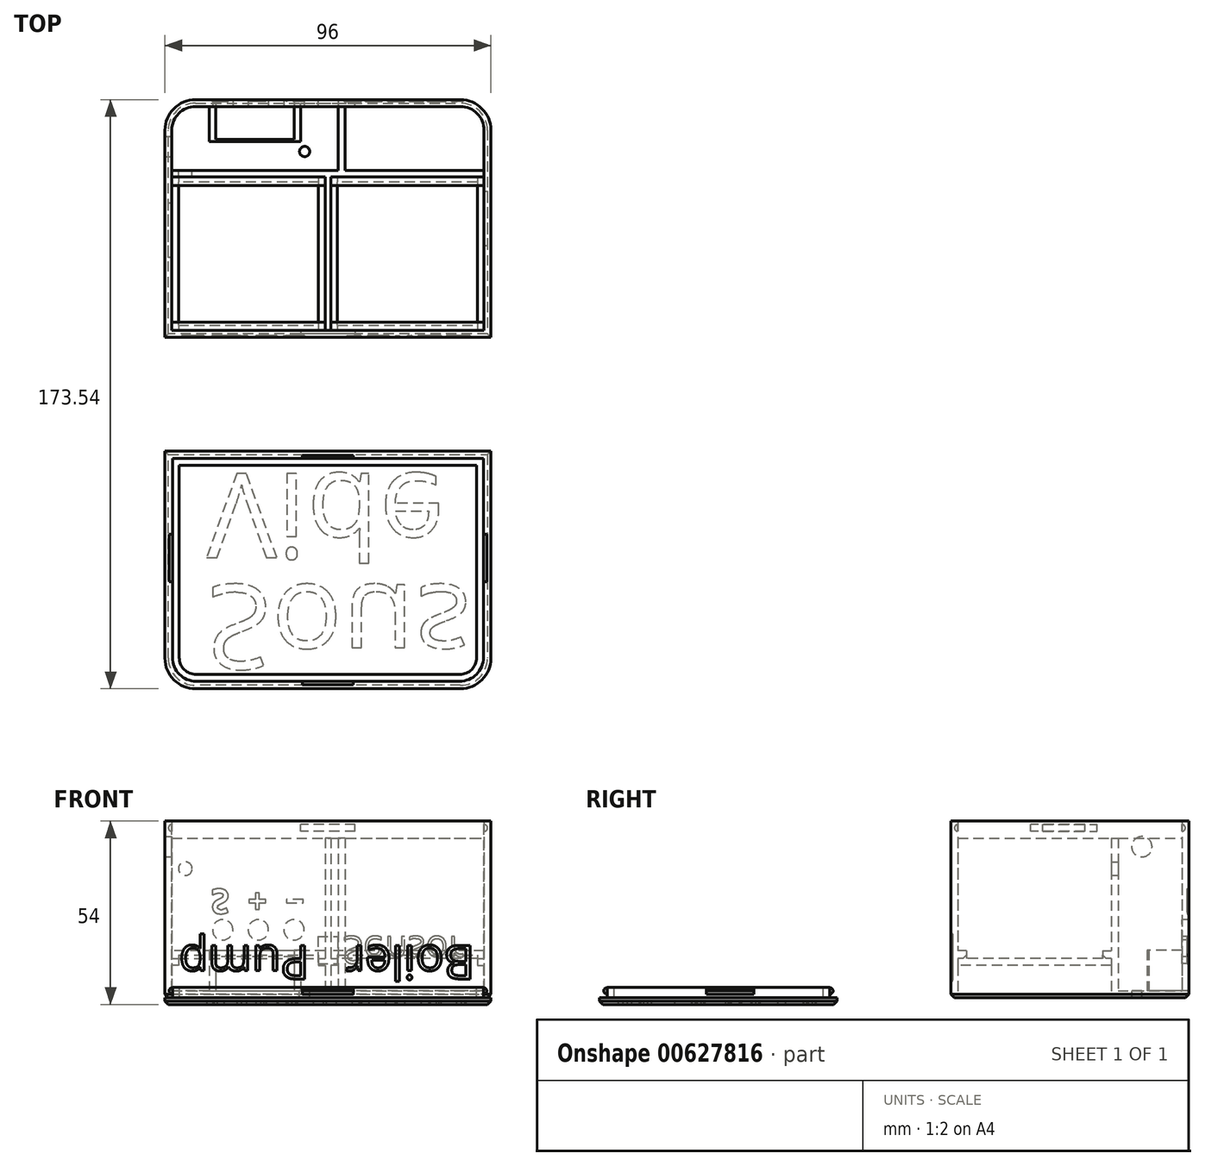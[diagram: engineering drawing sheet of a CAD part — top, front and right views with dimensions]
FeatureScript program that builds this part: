
annotation { "Feature Type Name" : "Feature", "Feature Type Description" : "" }
export const myFeature = defineFeature(function(context is Context, id is Id, definition is map)
    precondition{}
    {
        {
            var Q0;
            Q0=qCreatedBy(makeId("Top.planeOp"),FACE);
            var sketch = newSketch(context, id + "F0", { "sketchPlane" : qUnion([Q0])});
            skLineSegment(sketch, "E0.bottom", {"start": v(48, -35) * mm, "end": v(-48, -35) * mm});
            skLineSegment(sketch, "E0.top", {"start": v(48, 35) * mm, "end": v(-48, 35) * mm});
            skLineSegment(sketch, "E0.left", {"start": v(48, -35) * mm, "end": v(48, 35) * mm});
            skLineSegment(sketch, "E0.right", {"start": v(-48, -35) * mm, "end": v(-48, 35) * mm});
            skPoint(sketch, "E0.middle", {"position": v(0, 0) * mm});
            skLineSegment(sketch, "E1.bottom", {"start": v(48, -138.54) * mm, "end": v(-48, -138.54) * mm});
            skLineSegment(sketch, "E1.top", {"start": v(48, -68.54) * mm, "end": v(-48, -68.54) * mm});
            skLineSegment(sketch, "E1.left", {"start": v(48, -138.54) * mm, "end": v(48, -68.54) * mm});
            skLineSegment(sketch, "E1.right", {"start": v(-48, -138.54) * mm, "end": v(-48, -68.54) * mm});
            skPoint(sketch, "E1.middle", {"position": v(0, -103.54) * mm});
            skPoint(sketch, "E1.middle.positionSnap0", {"position": v(0, -35) * mm});
            skPoint(sketch, "E1.centerSnap0", {"position": v(0, -35) * mm});
            skLineSegment(sketch, "E2.bottom", {"start": v(45.8, -136.34) * mm, "end": v(-45.8, -136.34) * mm});
            skLineSegment(sketch, "E2.top", {"start": v(45.8, -70.74) * mm, "end": v(-45.8, -70.74) * mm});
            skLineSegment(sketch, "E2.left", {"start": v(45.8, -136.34) * mm, "end": v(45.8, -70.74) * mm});
            skLineSegment(sketch, "E2.right", {"start": v(-45.8, -136.34) * mm, "end": v(-45.8, -70.74) * mm});
            skSolve(sketch);
        }
        {
            var Q0;
            Q0=makeQuery(id+"F0.imprint","IMPRINT",FACE,{"disambiguationData":[TD([[makeQuery(id+"F0.imprint","IMPRINT",EDGE,{"derivedFrom":sQuery(id+"F0.wireOp",EDGE,"E0.bottom")}),-1.0]])]});
            extrude(context, id + "F1", {"entities" : qUnion([Q0]), "depth" : 52 * mm, "offsetDistance" : 25 * mm});
        }
        {
            var Q0;
            Q0=makeQuery(id+"F0.imprint","IMPRINT",FACE,{"disambiguationData":[TD([[makeQuery(id+"F0.imprint","IMPRINT",EDGE,{"derivedFrom":sQuery(id+"F0.wireOp",EDGE,"E1.bottom")}),-1.0]])]});
            var Q1;
            Q1=makeQuery(id+"F0.imprint","IMPRINT",FACE,{"disambiguationData":[TD([[makeQuery(id+"F0.imprint","IMPRINT",EDGE,{"derivedFrom":sQuery(id+"F0.wireOp",EDGE,"E2.bottom")}),-1.0]])]});
            extrude(context, id + "F2", {"entities" : qUnion([Q0, Q1]), "oppositeDirection" : true, "depth" : 2 * mm, "offsetDistance" : 25 * mm});
        }
        {
            var Q0;
            Q0=makeQuery(id+"F1.opExtrude","SWEPT_EDGE",EDGE,{"disambiguationData":[OSD([sQuery(id+"F0.wireOp",EDGE,"E0.top"),sQuery(id+"F0.wireOp",EDGE,"E0.right")])]});
            var Q1;
            Q1=makeQuery(id+"F1.opExtrude","SWEPT_EDGE",EDGE,{"disambiguationData":[OSD([sQuery(id+"F0.wireOp",EDGE,"E0.top"),sQuery(id+"F0.wireOp",EDGE,"E0.left")])]});
            var Q2;
            Q2=makeQuery(id+"F2.opExtrude","SWEPT_EDGE",EDGE,{"disambiguationData":[OSD([sQuery(id+"F0.wireOp",EDGE,"E1.bottom"),sQuery(id+"F0.wireOp",EDGE,"E1.right")])]});
            var Q3;
            Q3=makeQuery(id+"F2.opExtrude","SWEPT_EDGE",EDGE,{"disambiguationData":[OSD([sQuery(id+"F0.wireOp",EDGE,"E1.bottom"),sQuery(id+"F0.wireOp",EDGE,"E1.left")])]});
            fillet(context, id + "F3", {"entities" : qUnion([Q0, Q1, Q2, Q3]), "radius" : 9 * mm, "tangentPropagation" : true, "allowEdgeOverflow" : false});
        }
        {
            var Q0;
            Q0=makeQuery(id+"F1.opExtrude","CAP_FACE",FACE,{"disambiguationData":[OSD([sQuery(id+"F0.wireOp",EDGE,"E0.bottom"),sQuery(id+"F0.wireOp",EDGE,"E0.top"),sQuery(id+"F0.wireOp",EDGE,"E0.left"),sQuery(id+"F0.wireOp",EDGE,"E0.right")])],"isStart":false});
            shell(context, id + "F4", {"entities" : qUnion([Q0]), "thickness" : 2 * mm});
        }
        {
            var Q0;
            Q0=makeQuery(id+"F4.opShell","OFFSET_FACE",FACE,{"disambiguationData":[OSD([sQuery(id+"F0.wireOp",EDGE,"E0.bottom"),sQuery(id+"F0.wireOp",EDGE,"E0.top"),sQuery(id+"F0.wireOp",EDGE,"E0.left"),sQuery(id+"F0.wireOp",EDGE,"E0.right")])]});
            var sketch = newSketch(context, id + "F5", { "sketchPlane" : qUnion([Q0])});
            skLineSegment(sketch, "E3", {"start": v(-46, 12.2) * mm, "end": v(46, 12.2) * mm});
            skLineSegment(sketch, "E4", {"start": v(-46, 14.2) * mm, "end": v(46, 14.2) * mm});
            skLineSegment(sketch, "E5", {"start": v(3, 14.2) * mm, "end": v(3, 33) * mm});
            skLineSegment(sketch, "E6", {"start": v(5, 14.2) * mm, "end": v(5, 33) * mm});
            skLineSegment(sketch, "E7.bottom", {"start": v(-0.8, -33) * mm, "end": v(0.8, -33) * mm});
            skLineSegment(sketch, "E7.top", {"start": v(-0.8, 12.2) * mm, "end": v(0.8, 12.2) * mm});
            skLineSegment(sketch, "E7.left", {"start": v(-0.8, -33) * mm, "end": v(-0.8, 12.2) * mm});
            skLineSegment(sketch, "E7.right", {"start": v(0.8, -33) * mm, "end": v(0.8, 12.2) * mm});
            skLineSegment(sketch, "E8.bottom", {"start": v(-35, 33) * mm, "end": v(-33, 33) * mm});
            skLineSegment(sketch, "E8.top", {"start": v(-35, 22.7) * mm, "end": v(-33, 22.7) * mm});
            skLineSegment(sketch, "E8.left", {"start": v(-35, 33) * mm, "end": v(-35, 22.7) * mm});
            skLineSegment(sketch, "E8.right", {"start": v(-33, 33) * mm, "end": v(-33, 22.7) * mm});
            skLineSegment(sketch, "E9.bottom", {"start": v(-10, 33) * mm, "end": v(-8, 33) * mm});
            skLineSegment(sketch, "E9.top", {"start": v(-10, 22.7) * mm, "end": v(-8, 22.7) * mm});
            skLineSegment(sketch, "E9.left", {"start": v(-10, 33) * mm, "end": v(-10, 22.7) * mm});
            skLineSegment(sketch, "E9.right", {"start": v(-8, 33) * mm, "end": v(-8, 22.7) * mm});
            skLineSegment(sketch, "E10.bottom", {"start": v(-33, 23.25) * mm, "end": v(-10, 23.25) * mm});
            skLineSegment(sketch, "E10.top", {"start": v(-33, 22.7) * mm, "end": v(-10, 22.7) * mm});
            skLineSegment(sketch, "E10.left", {"start": v(-33, 23.25) * mm, "end": v(-33, 22.7) * mm});
            skLineSegment(sketch, "E10.right", {"start": v(-10, 23.25) * mm, "end": v(-10, 22.7) * mm});
            skPoint(sketch, "E11", {"position": v(-6.87, 19.74) * mm});
            skSolve(sketch);
        }
        {
            var Q0;
            {var subQ0=sQuery(id+"F5.wireOp",EDGE,"E3");Q0=makeQuery(id+"F5.imprint","IMPRINT",FACE,{"disambiguationData":[TD([[makeQuery(id+"F5.imprint","IMPRINT",EDGE,{"derivedFrom":subQ0}),1.0]])]});}
            var Q1;
            Q1=makeQuery(id+"F5.imprint","IMPRINT",FACE,{"disambiguationData":[TD([[makeQuery(id+"F5.imprint","IMPRINT",EDGE,{"derivedFrom":sQuery(id+"F5.wireOp",EDGE,"E7.bottom")}),-1.0]])]});
            var Q2;
            {var subQ0=sQuery(id+"F5.wireOp",EDGE,"E5");Q2=makeQuery(id+"F5.imprint","IMPRINT",FACE,{"disambiguationData":[TD([[makeQuery(id+"F5.imprint","IMPRINT",EDGE,{"derivedFrom":subQ0}),-1.0]])]});}
            extrude(context, id + "F6", {"entities" : qUnion([Q0, Q1, Q2]), "operationType" : NewBodyOperationType.ADD, "depth" : 45 * mm, "offsetDistance" : 25 * mm});
        }
        {
            var Q0;
            {var subQ0=sQuery(id+"F0.wireOp",EDGE,"E0.bottom");var subQ1=sQuery(id+"F0.wireOp",EDGE,"E0.left");var subQ2=sQuery(id+"F0.wireOp",EDGE,"E0.right");Q0=makeQuery(id+"F6.boolean.opBoolean","SPLIT",FACE,{"disambiguationData":[TD([makeQuery(id+"F4.opShell","OFFSET_FACE",FACE,{"disambiguationData":[OSD([subQ0])]})])],"derivedFrom":makeQuery(id+"F4.opShell","OFFSET_FACE",FACE,{"disambiguationData":[OSD([subQ0,sQuery(id+"F0.wireOp",EDGE,"E0.top"),subQ1,subQ2])]})});}
            extrude(context, id + "F7", {"entities" : qUnion([Q0]), "operationType" : NewBodyOperationType.REMOVE, "endBound" : BoundingType.UP_TO_NEXT, "oppositeDirection" : true, "depth" : 25 * mm, "offsetDistance" : 25 * mm});
        }
        {
            var Q0;
            {var subQ0=sQuery(id+"F0.wireOp",EDGE,"E0.right");Q0=makeQuery(id+"F7.boolean.opBoolean","MERGE",FACE,{"derivedFrom":[makeQuery(id+"F4.opShell","OFFSET_FACE",FACE,{"disambiguationData":[OSD([subQ0])]})],"fromTools":[makeQuery(id+"F7.opExtrude","SWEPT_FACE",FACE,{"disambiguationData":[OSD([subQ0])]})]});}
            var sketch = newSketch(context, id + "F8", { "sketchPlane" : qUnion([Q0])});
            skLineSegment(sketch, "E12.bottom", {"start": v(12.2, 11.5) * mm, "end": v(-33, 11.5) * mm});
            skLineSegment(sketch, "E12.top", {"start": v(12.2, 9.5) * mm, "end": v(-33, 9.5) * mm});
            skLineSegment(sketch, "E12.left", {"start": v(12.2, 11.5) * mm, "end": v(12.2, 9.5) * mm});
            skLineSegment(sketch, "E12.right", {"start": v(-33, 11.5) * mm, "end": v(-33, 9.5) * mm});
            skLineSegment(sketch, "E13", {"start": v(-3.5, 52) * mm, "end": v(-3.5, 50) * mm});
            skPoint(sketch, "E13.endSnap0", {"position": v(-3.5, 52) * mm});
            skLineSegment(sketch, "E14.bottom", {"start": v(4.5, 49) * mm, "end": v(-11.5, 49) * mm});
            skLineSegment(sketch, "E14.top", {"start": v(4.5, 51) * mm, "end": v(-11.5, 51) * mm});
            skLineSegment(sketch, "E14.left", {"start": v(4.5, 49) * mm, "end": v(4.5, 51) * mm});
            skLineSegment(sketch, "E14.right", {"start": v(-11.5, 49) * mm, "end": v(-11.5, 51) * mm});
            skPoint(sketch, "E14.middle", {"position": v(-3.5, 50) * mm});
            skPoint(sketch, "E15", {"position": v(21.2, 44.45) * mm});
            skPoint(sketch, "E16", {"position": v(19.78, 44.45) * mm});
            skSolve(sketch);
        }
        {
            var Q0;
            Q0=makeQuery(id+"F8.imprint","IMPRINT",FACE,{"disambiguationData":[TD([[makeQuery(id+"F8.imprint","IMPRINT",EDGE,{"derivedFrom":sQuery(id+"F8.wireOp",EDGE,"E12.bottom")}),1.0]])]});
            extrude(context, id + "F9", {"entities" : qUnion([Q0]), "operationType" : NewBodyOperationType.ADD, "depth" : 2 * mm, "offsetDistance" : 25 * mm});
        }
        {
            var Q0;
            {var subQ0=sQuery(id+"F5.wireOp",EDGE,"E7.left");Q0=makeQuery(id+"F7.boolean.opBoolean","MERGE",FACE,{"derivedFrom":[makeQuery(id+"F6.opExtrude","SWEPT_FACE",FACE,{"disambiguationData":[OSD([subQ0])]})],"fromTools":[makeQuery(id+"F7.opExtrude","SWEPT_FACE",FACE,{"disambiguationData":[OSD([subQ0])]})]});}
            var sketch = newSketch(context, id + "F10", { "sketchPlane" : qUnion([Q0])});
            skLineSegment(sketch, "E17.bottom", {"start": v(-12.2, 11.5) * mm, "end": v(33, 11.5) * mm});
            skLineSegment(sketch, "E17.top", {"start": v(-12.2, 9.5) * mm, "end": v(33, 9.5) * mm});
            skLineSegment(sketch, "E17.left", {"start": v(-12.2, 11.5) * mm, "end": v(-12.2, 9.5) * mm});
            skLineSegment(sketch, "E17.right", {"start": v(33, 11.5) * mm, "end": v(33, 9.5) * mm});
            skSolve(sketch);
        }
        {
            var Q0;
            Q0=makeQuery(id+"F10.imprint","IMPRINT",FACE,{"disambiguationData":[TD([[makeQuery(id+"F10.imprint","IMPRINT",EDGE,{"derivedFrom":sQuery(id+"F10.wireOp",EDGE,"E17.bottom")}),-1.0]])]});
            extrude(context, id + "F11", {"entities" : qUnion([Q0]), "operationType" : NewBodyOperationType.ADD, "depth" : 2 * mm, "offsetDistance" : 25 * mm});
        }
        {
            var Q0;
            {var subQ0=sQuery(id+"F5.wireOp",EDGE,"E7.right");Q0=makeQuery(id+"F7.boolean.opBoolean","MERGE",FACE,{"derivedFrom":[makeQuery(id+"F6.opExtrude","SWEPT_FACE",FACE,{"disambiguationData":[OSD([subQ0])]})],"fromTools":[makeQuery(id+"F7.opExtrude","SWEPT_FACE",FACE,{"disambiguationData":[OSD([subQ0])]})]});}
            var sketch = newSketch(context, id + "F12", { "sketchPlane" : qUnion([Q0])});
            skLineSegment(sketch, "E18.bottom", {"start": v(12.2, 9.5) * mm, "end": v(-33, 9.5) * mm});
            skLineSegment(sketch, "E18.top", {"start": v(12.2, 11.5) * mm, "end": v(-33, 11.5) * mm});
            skLineSegment(sketch, "E18.left", {"start": v(12.2, 9.5) * mm, "end": v(12.2, 11.5) * mm});
            skLineSegment(sketch, "E18.right", {"start": v(-33, 9.5) * mm, "end": v(-33, 11.5) * mm});
            skSolve(sketch);
        }
        {
            var Q0;
            Q0=makeQuery(id+"F12.imprint","IMPRINT",FACE,{"disambiguationData":[TD([[makeQuery(id+"F12.imprint","IMPRINT",EDGE,{"derivedFrom":sQuery(id+"F12.wireOp",EDGE,"E18.bottom")}),-1.0]])]});
            extrude(context, id + "F13", {"entities" : qUnion([Q0]), "operationType" : NewBodyOperationType.ADD, "depth" : 2 * mm, "offsetDistance" : 25 * mm});
        }
        {
            var Q0;
            {var subQ0=sQuery(id+"F0.wireOp",EDGE,"E0.left");Q0=makeQuery(id+"F7.boolean.opBoolean","MERGE",FACE,{"derivedFrom":[makeQuery(id+"F4.opShell","OFFSET_FACE",FACE,{"disambiguationData":[OSD([subQ0])]})],"fromTools":[makeQuery(id+"F7.opExtrude","SWEPT_FACE",FACE,{"disambiguationData":[OSD([subQ0])]})]});}
            var sketch = newSketch(context, id + "F14", { "sketchPlane" : qUnion([Q0])});
            skLineSegment(sketch, "E19.bottom", {"start": v(-12.2, 11.5) * mm, "end": v(33, 11.5) * mm});
            skLineSegment(sketch, "E19.top", {"start": v(-12.2, 9.5) * mm, "end": v(33, 9.5) * mm});
            skLineSegment(sketch, "E19.left", {"start": v(-12.2, 11.5) * mm, "end": v(-12.2, 9.5) * mm});
            skLineSegment(sketch, "E19.right", {"start": v(33, 11.5) * mm, "end": v(33, 9.5) * mm});
            skLineSegment(sketch, "E20", {"start": v(0, 52) * mm, "end": v(0, 50) * mm});
            skLineSegment(sketch, "E21.bottom", {"start": v(8, 49) * mm, "end": v(-8, 49) * mm});
            skLineSegment(sketch, "E21.top", {"start": v(8, 51) * mm, "end": v(-8, 51) * mm});
            skLineSegment(sketch, "E21.left", {"start": v(8, 49) * mm, "end": v(8, 51) * mm});
            skLineSegment(sketch, "E21.right", {"start": v(-8, 49) * mm, "end": v(-8, 51) * mm});
            skPoint(sketch, "E21.middle", {"position": v(0, 50) * mm});
            skSolve(sketch);
        }
        {
            var Q0;
            Q0=makeQuery(id+"F14.imprint","IMPRINT",FACE,{"disambiguationData":[TD([[makeQuery(id+"F14.imprint","IMPRINT",EDGE,{"derivedFrom":sQuery(id+"F14.wireOp",EDGE,"E19.bottom")}),-1.0]])]});
            extrude(context, id + "F15", {"entities" : qUnion([Q0]), "operationType" : NewBodyOperationType.ADD, "depth" : 2 * mm, "offsetDistance" : 25 * mm});
        }
        {
            var Q0;
            {var subQ0=sQuery(id+"F5.wireOp",EDGE,"E3");var subQ1=sQuery(id+"F0.wireOp",EDGE,"E0.right");var subQ2=makeQuery(id+"F5.imprint","IMPRINT",EDGE,{"disambiguationData":[TD([[makeQuery(id+"F5.imprint","INTERSECT",VERTEX,{"derivedFrom":[makeQuery(id+"F4.opShell","OFFSET_EDGE",EDGE,{"disambiguationData":[OSD([subQ1]),TDD([makeQuery(id+"F1.opExtrude","CAP_EDGE",EDGE,{"disambiguationData":[OSD([subQ1])],"isStart":true})])]}),subQ0]}),-1.0]])],"derivedFrom":subQ0});Q0=makeQuery(id+"F7.boolean.opBoolean","MERGE",FACE,{"derivedFrom":[makeQuery(id+"F6.opExtrude","SWEPT_FACE",FACE,{"disambiguationData":[OSD([subQ0]),TDD([subQ2])]})],"fromTools":[makeQuery(id+"F7.opExtrude","SWEPT_FACE",FACE,{"disambiguationData":[OSD([subQ0]),TDD([makeQuery(id+"F6.opExtrude","CAP_EDGE",EDGE,{"disambiguationData":[OSD([subQ0]),TDD([subQ2])],"isStart":true})])]})]});}
            var sketch = newSketch(context, id + "F16", { "sketchPlane" : qUnion([Q0])});
            skLineSegment(sketch, "E22.bottom", {"start": v(-46, 11.5) * mm, "end": v(-0.8, 11.5) * mm});
            skLineSegment(sketch, "E22.top", {"start": v(-46, 13.8) * mm, "end": v(-0.8, 13.8) * mm});
            skLineSegment(sketch, "E22.left", {"start": v(-46, 11.5) * mm, "end": v(-46, 13.8) * mm});
            skLineSegment(sketch, "E22.right", {"start": v(-0.8, 11.5) * mm, "end": v(-0.8, 13.8) * mm});
            skSolve(sketch);
        }
        {
            var Q0;
            Q0=makeQuery(id+"F16.imprint","IMPRINT",FACE,{"disambiguationData":[TD([[makeQuery(id+"F16.imprint","IMPRINT",EDGE,{"derivedFrom":sQuery(id+"F16.wireOp",EDGE,"E22.bottom")}),1.0]])]});
            extrude(context, id + "F17", {"entities" : qUnion([Q0]), "operationType" : NewBodyOperationType.ADD, "depth" : 2.5 * mm, "offsetDistance" : 25 * mm});
        }
        {
            var Q0;
            {var subQ0=sQuery(id+"F5.wireOp",EDGE,"E3");var subQ1=sQuery(id+"F0.wireOp",EDGE,"E0.left");var subQ2=makeQuery(id+"F5.imprint","IMPRINT",EDGE,{"disambiguationData":[TD([[makeQuery(id+"F5.imprint","INTERSECT",VERTEX,{"derivedFrom":[makeQuery(id+"F4.opShell","OFFSET_EDGE",EDGE,{"disambiguationData":[OSD([subQ1]),TDD([makeQuery(id+"F1.opExtrude","CAP_EDGE",EDGE,{"disambiguationData":[OSD([subQ1])],"isStart":true})])]}),subQ0]}),1.0]])],"derivedFrom":subQ0});Q0=makeQuery(id+"F7.boolean.opBoolean","MERGE",FACE,{"derivedFrom":[makeQuery(id+"F6.opExtrude","SWEPT_FACE",FACE,{"disambiguationData":[OSD([subQ0]),TDD([subQ2])]})],"fromTools":[makeQuery(id+"F7.opExtrude","SWEPT_FACE",FACE,{"disambiguationData":[OSD([subQ0]),TDD([makeQuery(id+"F6.opExtrude","CAP_EDGE",EDGE,{"disambiguationData":[OSD([subQ0]),TDD([subQ2])],"isStart":true})])]})]});}
            var sketch = newSketch(context, id + "F18", { "sketchPlane" : qUnion([Q0])});
            skLineSegment(sketch, "E23.bottom", {"start": v(0.8, 11.5) * mm, "end": v(46, 11.5) * mm});
            skLineSegment(sketch, "E23.top", {"start": v(0.8, 13.8) * mm, "end": v(46, 13.8) * mm});
            skLineSegment(sketch, "E23.left", {"start": v(0.8, 11.5) * mm, "end": v(0.8, 13.8) * mm});
            skLineSegment(sketch, "E23.right", {"start": v(46, 11.5) * mm, "end": v(46, 13.8) * mm});
            skSolve(sketch);
        }
        {
            var Q0;
            Q0=makeQuery(id+"F18.imprint","IMPRINT",FACE,{"disambiguationData":[TD([[makeQuery(id+"F18.imprint","IMPRINT",EDGE,{"derivedFrom":sQuery(id+"F18.wireOp",EDGE,"E23.top")}),-1.0]])]});
            extrude(context, id + "F19", {"entities" : qUnion([Q0]), "operationType" : NewBodyOperationType.ADD, "depth" : 2.5 * mm, "offsetDistance" : 25 * mm});
        }
        {
            var Q0;
            {var subQ0=sQuery(id+"F0.wireOp",EDGE,"E0.bottom");var subQ1=makeQuery(id+"F4.opShell","OFFSET_FACE",FACE,{"disambiguationData":[OSD([subQ0])]});var subQ2=sQuery(id+"F0.wireOp",EDGE,"E0.right");var subQ3=sQuery(id+"F0.wireOp",EDGE,"E0.left");var subQ5=makeQuery(id+"F4.opShell","OFFSET_EDGE",EDGE,{"disambiguationData":[OSD([subQ0]),TDD([makeQuery(id+"F1.opExtrude","CAP_EDGE",EDGE,{"disambiguationData":[OSD([subQ0])],"isStart":true})])]});Q0=makeQuery(id+"F7.boolean.opBoolean","MERGE",FACE,{"derivedFrom":[subQ1],"fromTools":[makeQuery(id+"F7.opExtrude","SWEPT_FACE",FACE,{"disambiguationData":[OSD([subQ0]),TDD([makeQuery(id+"F6.boolean.opBoolean","SPLIT",EDGE,{"disambiguationData":[TD([makeQuery(id+"F4.opShell","OFFSET_FACE",FACE,{"disambiguationData":[OSD([subQ3])]})])],"derivedFrom":subQ5})])]}),makeQuery(id+"F7.opExtrude","SWEPT_FACE",FACE,{"disambiguationData":[OSD([subQ0]),TDD([makeQuery(id+"F6.boolean.opBoolean","SPLIT",EDGE,{"disambiguationData":[TD([makeQuery(id+"F4.opShell","OFFSET_FACE",FACE,{"disambiguationData":[OSD([subQ2])]})])],"derivedFrom":subQ5})])]})]});}
            var sketch = newSketch(context, id + "F20", { "sketchPlane" : qUnion([Q0])});
            skLineSegment(sketch, "E24.bottom", {"start": v(-46, 13.8) * mm, "end": v(46, 13.8) * mm});
            skLineSegment(sketch, "E24.top", {"start": v(-46, 11.5) * mm, "end": v(46, 11.5) * mm});
            skLineSegment(sketch, "E24.left", {"start": v(-46, 13.8) * mm, "end": v(-46, 11.5) * mm});
            skLineSegment(sketch, "E24.right", {"start": v(46, 13.8) * mm, "end": v(46, 11.5) * mm});
            skLineSegment(sketch, "E25", {"start": v(0, 52) * mm, "end": v(0, 50) * mm});
            skLineSegment(sketch, "E26.bottom", {"start": v(8, 49) * mm, "end": v(-8, 49) * mm});
            skLineSegment(sketch, "E26.top", {"start": v(8, 51) * mm, "end": v(-8, 51) * mm});
            skLineSegment(sketch, "E26.left", {"start": v(8, 49) * mm, "end": v(8, 51) * mm});
            skLineSegment(sketch, "E26.right", {"start": v(-8, 49) * mm, "end": v(-8, 51) * mm});
            skPoint(sketch, "E26.middle", {"position": v(0, 50) * mm});
            skSolve(sketch);
        }
        {
            var Q0;
            {var subQ21=sQuery(id+"F20.wireOp",EDGE,"E24.right");Q0=makeQuery(id+"F20.imprint","IMPRINT",FACE,{"disambiguationData":[TD([[makeQuery(id+"F20.imprint","IMPRINT",EDGE,{"derivedFrom":subQ21}),-1.0]])]});}
            var Q1;
            {var subQ19=sQuery(id+"F20.wireOp",EDGE,"E24.left");Q1=makeQuery(id+"F20.imprint","IMPRINT",FACE,{"disambiguationData":[TD([[makeQuery(id+"F20.imprint","IMPRINT",EDGE,{"derivedFrom":subQ19}),1.0]])]});}
            extrude(context, id + "F21", {"entities" : qUnion([Q0, Q1]), "operationType" : NewBodyOperationType.ADD, "depth" : 2.5 * mm, "offsetDistance" : 25 * mm});
        }
        {
            var Q0;
            Q0=makeQuery(id+"F1.opExtrude","SWEPT_FACE",FACE,{"disambiguationData":[OSD([sQuery(id+"F0.wireOp",EDGE,"E0.bottom")])]});
            var sketch = newSketch(context, id + "F22", { "sketchPlane" : qUnion([Q0])});
            skText(sketch, "E27", { "text": "Boiler   Pump", "fontName": "OpenSans-Regular.ttf"});
            const initialGuessF22  = {"E27": [0.04318, 0.0154, -1, 0, 0.01]};
            skSetInitialGuess(sketch, initialGuessF22);
            skSolve(sketch);
        }
        {
            var Q0;
            Q0 = qSketchRegion(id + "F22", true);
            extrude(context, id + "F23", {"entities" : qUnion([Q0]), "operationType" : NewBodyOperationType.REMOVE, "oppositeDirection" : true, "depth" : 0.5 * mm, "offsetDistance" : 25 * mm});
        }
        {
            var Q0;
            Q0=makeQuery(id+"F4.opShell","OFFSET_FACE",FACE,{"disambiguationData":[OSD([sQuery(id+"F0.wireOp",EDGE,"E0.top")])]});
            var sketch = newSketch(context, id + "F24", { "sketchPlane" : qUnion([Q0])});
            skLineSegment(sketch, "E28.bottom", {"start": v(3, 10) * mm, "end": v(-3, 10) * mm});
            skLineSegment(sketch, "E28.top", {"start": v(3, 18) * mm, "end": v(-3, 18) * mm});
            skLineSegment(sketch, "E28.left", {"start": v(3, 10) * mm, "end": v(3, 18) * mm});
            skLineSegment(sketch, "E28.right", {"start": v(-3, 10) * mm, "end": v(-3, 18) * mm});
            skLineSegment(sketch, "E29.bottom", {"start": v(-33, 2) * mm, "end": v(-10, 2) * mm});
            skLineSegment(sketch, "E29.top", {"start": v(-33, 12) * mm, "end": v(-10, 12) * mm});
            skLineSegment(sketch, "E29.left", {"start": v(-33, 2) * mm, "end": v(-33, 12) * mm});
            skLineSegment(sketch, "E29.right", {"start": v(-10, 2) * mm, "end": v(-10, 12) * mm});
            skPoint(sketch, "E30", {"position": v(-10, 20) * mm});
            skPoint(sketch, "E31", {"position": v(-20.5, 20) * mm});
            skPoint(sketch, "E32", {"position": v(-31, 20) * mm});
            skLineSegment(sketch, "E33", {"start": v(0, 52) * mm, "end": v(0, 50) * mm});
            skPoint(sketch, "E33.endSnap0", {"position": v(0, 52) * mm});
            skLineSegment(sketch, "E34.bottom", {"start": v(8, 49) * mm, "end": v(-8, 49) * mm});
            skLineSegment(sketch, "E34.top", {"start": v(8, 51) * mm, "end": v(-8, 51) * mm});
            skLineSegment(sketch, "E34.left", {"start": v(8, 49) * mm, "end": v(8, 51) * mm});
            skLineSegment(sketch, "E34.right", {"start": v(-8, 49) * mm, "end": v(-8, 51) * mm});
            skPoint(sketch, "E34.middle", {"position": v(0, 50) * mm});
            skSolve(sketch);
        }
        {
            var Q0;
            Q0=makeQuery(id+"F24.imprint","IMPRINT",FACE,{"disambiguationData":[TD([[makeQuery(id+"F24.imprint","IMPRINT",EDGE,{"derivedFrom":sQuery(id+"F24.wireOp",EDGE,"E28.bottom")}),-1.0]])]});
            var Q1;
            Q1=makeQuery(id+"F24.imprint","IMPRINT",FACE,{"disambiguationData":[TD([[makeQuery(id+"F24.imprint","IMPRINT",EDGE,{"derivedFrom":sQuery(id+"F24.wireOp",EDGE,"E29.bottom")}),-1.0]])]});
            extrude(context, id + "F25", {"entities" : qUnion([Q0, Q1]), "operationType" : NewBodyOperationType.REMOVE, "endBound" : BoundingType.UP_TO_NEXT, "oppositeDirection" : true, "depth" : 25 * mm, "offsetDistance" : 25 * mm});
        }
        {
            var Q0;
            Q0=makeQuery(id+"F5.imprint","IMPRINT",FACE,{"disambiguationData":[TD([[makeQuery(id+"F5.imprint","IMPRINT",EDGE,{"derivedFrom":sQuery(id+"F5.wireOp",EDGE,"E8.bottom")}),1.0]])]});
            var Q1;
            {var subQ3=sQuery(id+"F5.wireOp",EDGE,"E9.bottom");Q1=makeQuery(id+"F5.imprint","IMPRINT",FACE,{"disambiguationData":[TD([[makeQuery(id+"F5.imprint","IMPRINT",EDGE,{"derivedFrom":subQ3}),1.0]])]});}
            var Q2;
            Q2=makeQuery(id+"F5.imprint","IMPRINT",FACE,{"disambiguationData":[TD([[makeQuery(id+"F5.imprint","IMPRINT",EDGE,{"derivedFrom":sQuery(id+"F5.wireOp",EDGE,"E10.bottom")}),-1.0]])]});
            extrude(context, id + "F26", {"entities" : qUnion([Q0, Q1, Q2]), "operationType" : NewBodyOperationType.ADD, "depth" : 12 * mm, "offsetDistance" : 25 * mm});
        }
        {
            var Q0;
            Q0=sQuery(id+"F24.wireOp",VERTEX,"E32");
            var Q1;
            Q1=sQuery(id+"F24.wireOp",VERTEX,"E31");
            var Q2;
            Q2=sQuery(id+"F24.wireOp",VERTEX,"E30");
            var Q3;
            Q3=makeQuery(id+"F1.opExtrude","SWEPT_BODY",BODY,{"disambiguationData":[OSD([sQuery(id+"F0.wireOp",EDGE,"E0.bottom"),sQuery(id+"F0.wireOp",EDGE,"E0.top"),sQuery(id+"F0.wireOp",EDGE,"E0.left"),sQuery(id+"F0.wireOp",EDGE,"E0.right")])]});
            hole(context, id + "F27", {"style" : HoleStyle.SIMPLE, "endStyle" : HoleEndStyle.THROUGH, "holeDiameter" : 6 * mm, "majorDiameter" : 5 * mm, "isTappedThrough" : true, "tappedDepth" : 12 * mm, "tapClearance" : 3, "locations" : qUnion([Q0, Q1, Q2]), "scope" : qUnion([Q3])});
        }
        {
            var Q0;
            Q0=makeQuery(id+"F1.opExtrude","SWEPT_FACE",FACE,{"disambiguationData":[OSD([sQuery(id+"F0.wireOp",EDGE,"E0.top")])]});
            var sketch = newSketch(context, id + "F28", { "sketchPlane" : qUnion([Q0])});
            skText(sketch, "E35", { "text": "S  +  −", "fontName": "OpenSans-Bold.ttf"});
            skText(sketch, "E36", { "text": "Sensor", "fontName": "OpenSans-Regular.ttf"});
            const initialGuessF28  = {"E35": [0.03457, 0.032, -1, 0, 0.0073], "E36": [-0.00427, 0.01805, -1, 0, 0.008]};
            skSetInitialGuess(sketch, initialGuessF28);
            skSolve(sketch);
        }
        {
            var Q0;
            Q0 = qSketchRegion(id + "F28", true);
            extrude(context, id + "F29", {"entities" : qUnion([Q0]), "operationType" : NewBodyOperationType.REMOVE, "oppositeDirection" : true, "depth" : 0.5 * mm, "offsetDistance" : 25 * mm});
        }
        {
            var Q0;
            {var subQ0=sQuery(id+"F5.wireOp",EDGE,"E4");Q0=makeQuery(id+"F6.opExtrude","SWEPT_FACE",FACE,{"disambiguationData":[OSD([subQ0]),TDD([makeQuery(id+"F5.imprint","IMPRINT",EDGE,{"disambiguationData":[TD([[makeQuery(id+"F5.imprint","INTERSECT",VERTEX,{"derivedFrom":[subQ0,sQuery(id+"F5.wireOp",EDGE,"E5")]}),1.0]])],"derivedFrom":subQ0})])]});}
            var sketch = newSketch(context, id + "F30", { "sketchPlane" : qUnion([Q0])});
            skPoint(sketch, "E37", {"position": v(42, 38) * mm});
            skSolve(sketch);
        }
        {
            var Q0;
            Q0=sQuery(id+"F30.wireOp",VERTEX,"E37");
            var Q1;
            Q1=makeQuery(id+"F1.opExtrude","SWEPT_BODY",BODY,{"disambiguationData":[OSD([sQuery(id+"F0.wireOp",EDGE,"E0.bottom"),sQuery(id+"F0.wireOp",EDGE,"E0.top"),sQuery(id+"F0.wireOp",EDGE,"E0.left"),sQuery(id+"F0.wireOp",EDGE,"E0.right")])]});
            hole(context, id + "F31", {"style" : HoleStyle.SIMPLE, "endStyle" : HoleEndStyle.BLIND, "holeDiameter" : 4 * mm, "majorDiameter" : 5 * mm, "holeDepth" : 20 * mm, "isTappedThrough" : true, "tappedDepth" : 12 * mm, "tapClearance" : 3, "locations" : qUnion([Q0]), "scope" : qUnion([Q1])});
        }
        {
            var Q0;
            Q0=makeQuery(id+"F24.imprint","IMPRINT",FACE,{"disambiguationData":[TD([[makeQuery(id+"F24.imprint","IMPRINT",EDGE,{"derivedFrom":sQuery(id+"F24.wireOp",EDGE,"E34.bottom")}),-1.0]])]});
            extrude(context, id + "F32", {"entities" : qUnion([Q0]), "operationType" : NewBodyOperationType.REMOVE, "oppositeDirection" : true, "depth" : 1 * mm, "offsetDistance" : 25 * mm});
        }
        {
            var Q0;
            Q0=makeQuery(id+"F8.imprint","IMPRINT",FACE,{"disambiguationData":[TD([[makeQuery(id+"F8.imprint","IMPRINT",EDGE,{"derivedFrom":sQuery(id+"F8.wireOp",EDGE,"E14.bottom")}),-1.0]])]});
            extrude(context, id + "F33", {"entities" : qUnion([Q0]), "operationType" : NewBodyOperationType.REMOVE, "oppositeDirection" : true, "depth" : 1 * mm, "offsetDistance" : 25 * mm});
        }
        {
            var Q0;
            Q0=makeQuery(id+"F20.imprint","IMPRINT",FACE,{"disambiguationData":[TD([[makeQuery(id+"F20.imprint","IMPRINT",EDGE,{"derivedFrom":sQuery(id+"F20.wireOp",EDGE,"E26.bottom")}),-1.0]])]});
            extrude(context, id + "F34", {"entities" : qUnion([Q0]), "operationType" : NewBodyOperationType.REMOVE, "oppositeDirection" : true, "depth" : 1 * mm, "offsetDistance" : 25 * mm});
        }
        {
            var Q0;
            Q0=makeQuery(id+"F14.imprint","IMPRINT",FACE,{"disambiguationData":[TD([[makeQuery(id+"F14.imprint","IMPRINT",EDGE,{"derivedFrom":sQuery(id+"F14.wireOp",EDGE,"E21.bottom")}),-1.0]])]});
            extrude(context, id + "F35", {"entities" : qUnion([Q0]), "operationType" : NewBodyOperationType.REMOVE, "oppositeDirection" : true, "depth" : 1 * mm, "offsetDistance" : 25 * mm});
        }
        {
            var Q0;
            Q0=sQuery(id+"F8.wireOp",VERTEX,"E15");
            var Q1;
            Q1=makeQuery(id+"F1.opExtrude","SWEPT_BODY",BODY,{"disambiguationData":[OSD([sQuery(id+"F0.wireOp",EDGE,"E0.bottom"),sQuery(id+"F0.wireOp",EDGE,"E0.top"),sQuery(id+"F0.wireOp",EDGE,"E0.left"),sQuery(id+"F0.wireOp",EDGE,"E0.right")])]});
            hole(context, id + "F36", {"style" : HoleStyle.SIMPLE, "endStyle" : HoleEndStyle.THROUGH, "holeDiameter" : 6 * mm, "majorDiameter" : 5 * mm, "isTappedThrough" : true, "tappedDepth" : 12 * mm, "tapClearance" : 3, "locations" : qUnion([Q0]), "scope" : qUnion([Q1])});
        }
        {
            var Q0;
            Q0=sQuery(id+"F5.wireOp",VERTEX,"E11");
            var Q1;
            Q1=makeQuery(id+"F1.opExtrude","SWEPT_BODY",BODY,{"disambiguationData":[OSD([sQuery(id+"F0.wireOp",EDGE,"E0.bottom"),sQuery(id+"F0.wireOp",EDGE,"E0.top"),sQuery(id+"F0.wireOp",EDGE,"E0.left"),sQuery(id+"F0.wireOp",EDGE,"E0.right")])]});
            hole(context, id + "F37", {"style" : HoleStyle.SIMPLE, "endStyle" : HoleEndStyle.THROUGH, "holeDiameter" : 3 * mm, "majorDiameter" : 5 * mm, "isTappedThrough" : true, "tappedDepth" : 12 * mm, "tapClearance" : 3, "locations" : qUnion([Q0]), "scope" : qUnion([Q1])});
        }
        {
            var Q0;
            Q0=makeQuery(id+"F0.imprint","IMPRINT",FACE,{"disambiguationData":[TD([[makeQuery(id+"F0.imprint","IMPRINT",EDGE,{"derivedFrom":sQuery(id+"F0.wireOp",EDGE,"E2.bottom")}),-1.0]])]});
            extrude(context, id + "F38", {"entities" : qUnion([Q0]), "operationType" : NewBodyOperationType.ADD, "depth" : 3 * mm, "offsetDistance" : 25 * mm});
        }
        {
            var Q0;
            Q0=makeQuery(id+"F38.opExtrude","SWEPT_EDGE",EDGE,{"disambiguationData":[OSD([sQuery(id+"F0.wireOp",EDGE,"E2.bottom"),sQuery(id+"F0.wireOp",EDGE,"E2.right")])]});
            var Q1;
            Q1=makeQuery(id+"F38.opExtrude","SWEPT_EDGE",EDGE,{"disambiguationData":[OSD([sQuery(id+"F0.wireOp",EDGE,"E2.bottom"),sQuery(id+"F0.wireOp",EDGE,"E2.left")])]});
            fillet(context, id + "F39", {"entities" : qUnion([Q0, Q1]), "radius" : 7 * mm, "tangentPropagation" : true, "allowEdgeOverflow" : false});
        }
        {
            var Q0;
            Q0=makeQuery(id+"F38.opExtrude","CAP_FACE",FACE,{"disambiguationData":[OSD([sQuery(id+"F0.wireOp",EDGE,"E2.bottom"),sQuery(id+"F0.wireOp",EDGE,"E2.top"),sQuery(id+"F0.wireOp",EDGE,"E2.left"),sQuery(id+"F0.wireOp",EDGE,"E2.right")])],"isStart":false});
            shell(context, id + "F40", {"entities" : qUnion([Q0]), "thickness" : 2 * mm});
        }
        {
            var Q0;
            Q0=makeQuery(id+"F1.opExtrude","CAP_EDGE",EDGE,{"disambiguationData":[OSD([sQuery(id+"F0.wireOp",EDGE,"E0.bottom")])],"isStart":true});
            var Q1;
            Q1=makeQuery(id+"F1.opExtrude","CAP_EDGE",EDGE,{"disambiguationData":[OSD([sQuery(id+"F0.wireOp",EDGE,"E0.right")])],"isStart":true});
            var Q2;
            Q2=makeQuery(id+"F1.opExtrude","CAP_EDGE",EDGE,{"disambiguationData":[OSD([sQuery(id+"F0.wireOp",EDGE,"E0.top")])],"isStart":true});
            var Q3;
            Q3=makeQuery(id+"F1.opExtrude","CAP_EDGE",EDGE,{"disambiguationData":[OSD([sQuery(id+"F0.wireOp",EDGE,"E0.left")])],"isStart":true});
            var Q4;
            {var subQ0=sQuery(id+"F16.wireOp",EDGE,"E22.bottom");Q4=makeQuery(id+"F17.boolean.opBoolean","SPLIT",EDGE,{"disambiguationData":[topologyDisambiguationEdgeConnected([makeQuery(id+"F17.opExtrude","SWEPT_FACE",FACE,{"disambiguationData":[OSD([subQ0])]})])],"derivedFrom":makeQuery(id+"F17.opExtrude","CAP_EDGE",EDGE,{"disambiguationData":[OSD([subQ0])],"isStart":false})});}
            var Q5;
            {var subQ0=sQuery(id+"F18.wireOp",EDGE,"E23.bottom");Q5=makeQuery(id+"F19.boolean.opBoolean","SPLIT",EDGE,{"disambiguationData":[topologyDisambiguationEdgeConnected([makeQuery(id+"F19.opExtrude","SWEPT_FACE",FACE,{"disambiguationData":[OSD([subQ0])]})])],"derivedFrom":makeQuery(id+"F19.opExtrude","CAP_EDGE",EDGE,{"disambiguationData":[OSD([subQ0])],"isStart":false})});}
            var Q6;
            {var subQ0=sQuery(id+"F20.wireOp",EDGE,"E24.left");var subQ1=sQuery(id+"F20.wireOp",EDGE,"E24.top");var subQ2=sQuery(id+"F5.wireOp",EDGE,"E7.right");var subQ3=sQuery(id+"F5.wireOp",EDGE,"E7.bottom");var subQ4=sQuery(id+"F0.wireOp",EDGE,"E0.bottom");var subQ5=makeQuery(id+"F20.imprint","INTERSECT",VERTEX,{"derivedFrom":[makeQuery(id+"F13.opExtrude","CAP_EDGE",EDGE,{"disambiguationData":[OSD([sQuery(id+"F12.wireOp",EDGE,"E18.right")])],"isStart":false}),subQ1]});var subQ6=makeQuery(id+"F20.imprint","IMPRINT",EDGE,{"disambiguationData":[TD([[makeQuery(id+"F20.imprint","INTERSECT",VERTEX,{"derivedFrom":[makeQuery(id+"F13.boolean.opBoolean","SPLIT",EDGE,{"disambiguationData":[TD([makeQuery(id+"F13.opExtrude","SWEPT_FACE",FACE,{"disambiguationData":[OSD([sQuery(id+"F12.wireOp",EDGE,"E18.top")])]})])],"derivedFrom":makeQuery(id+"F7.boolean.opBoolean","MERGE",EDGE,{"derivedFrom":[makeQuery(id+"F6.opExtrude","SWEPT_EDGE",EDGE,{"disambiguationData":[OSD([subQ4,subQ3,subQ2])]})],"fromTools":[makeQuery(id+"F7.opExtrude","SWEPT_EDGE",EDGE,{"disambiguationData":[OSD([subQ4,subQ3,subQ2])]})]})}),subQ1]}),1.0],[subQ5,-1.0]])],"derivedFrom":subQ1});var subQ7=makeQuery(id+"F20.imprint","INTERSECT",VERTEX,{"derivedFrom":[makeQuery(id+"F15.opExtrude","CAP_EDGE",EDGE,{"disambiguationData":[OSD([sQuery(id+"F14.wireOp",EDGE,"E19.right")])],"isStart":false}),subQ1]});var subQ8=makeQuery(id+"F20.imprint","IMPRINT",EDGE,{"disambiguationData":[TD([[makeQuery(id+"F20.imprint","INTERSECT",VERTEX,{"derivedFrom":[subQ1,subQ0]}),1.0],[subQ7,-1.0]])],"derivedFrom":subQ1});var subQ9=makeQuery(id+"F20.imprint","IMPRINT",EDGE,{"disambiguationData":[TD([[subQ5,1.0],[subQ7,-1.0]])],"derivedFrom":subQ1});Q6=makeQuery(id+"F21.boolean.opBoolean","SPLIT",EDGE,{"disambiguationData":[topologyDisambiguationEdgeConnected([makeQuery(id+"F21.opExtrude","SWEPT_FACE",FACE,{"disambiguationData":[OSD([subQ1]),TDD([subQ9,subQ8,subQ6])]})])],"derivedFrom":makeQuery(id+"F21.opExtrude","CAP_EDGE",EDGE,{"disambiguationData":[OSD([subQ1]),TDD([subQ9,subQ8,subQ6])],"isStart":false})});}
            var Q7;
            {var subQ0=sQuery(id+"F20.wireOp",EDGE,"E24.right");var subQ1=sQuery(id+"F20.wireOp",EDGE,"E24.top");var subQ2=sQuery(id+"F5.wireOp",EDGE,"E7.left");var subQ3=sQuery(id+"F5.wireOp",EDGE,"E7.bottom");var subQ4=sQuery(id+"F0.wireOp",EDGE,"E0.bottom");var subQ5=makeQuery(id+"F20.imprint","INTERSECT",VERTEX,{"derivedFrom":[makeQuery(id+"F9.opExtrude","CAP_EDGE",EDGE,{"disambiguationData":[OSD([sQuery(id+"F8.wireOp",EDGE,"E12.right")])],"isStart":false}),subQ1]});var subQ6=makeQuery(id+"F20.imprint","INTERSECT",VERTEX,{"derivedFrom":[makeQuery(id+"F11.opExtrude","CAP_EDGE",EDGE,{"disambiguationData":[OSD([sQuery(id+"F10.wireOp",EDGE,"E17.right")])],"isStart":false}),subQ1]});var subQ7=makeQuery(id+"F20.imprint","IMPRINT",EDGE,{"disambiguationData":[TD([[subQ5,1.0],[subQ6,-1.0]])],"derivedFrom":subQ1});var subQ8=makeQuery(id+"F20.imprint","IMPRINT",EDGE,{"disambiguationData":[TD([[makeQuery(id+"F20.imprint","INTERSECT",VERTEX,{"derivedFrom":[subQ1,subQ0]}),1.0],[subQ5,-1.0]])],"derivedFrom":subQ1});var subQ9=makeQuery(id+"F20.imprint","IMPRINT",EDGE,{"disambiguationData":[TD([[makeQuery(id+"F20.imprint","INTERSECT",VERTEX,{"derivedFrom":[makeQuery(id+"F11.boolean.opBoolean","SPLIT",EDGE,{"disambiguationData":[TD([makeQuery(id+"F11.opExtrude","SWEPT_FACE",FACE,{"disambiguationData":[OSD([sQuery(id+"F10.wireOp",EDGE,"E17.bottom")])]})])],"derivedFrom":makeQuery(id+"F7.boolean.opBoolean","MERGE",EDGE,{"derivedFrom":[makeQuery(id+"F6.opExtrude","SWEPT_EDGE",EDGE,{"disambiguationData":[OSD([subQ4,subQ3,subQ2])]})],"fromTools":[makeQuery(id+"F7.opExtrude","SWEPT_EDGE",EDGE,{"disambiguationData":[OSD([subQ4,subQ3,subQ2])]})]})}),subQ1]}),1.0],[subQ6,-1.0]])],"derivedFrom":subQ1});Q7=makeQuery(id+"F21.boolean.opBoolean","SPLIT",EDGE,{"disambiguationData":[topologyDisambiguationEdgeConnected([makeQuery(id+"F21.opExtrude","SWEPT_FACE",FACE,{"disambiguationData":[OSD([subQ1]),TDD([subQ9,subQ8,subQ7])]})])],"derivedFrom":makeQuery(id+"F21.opExtrude","CAP_EDGE",EDGE,{"disambiguationData":[OSD([subQ1]),TDD([subQ9,subQ8,subQ7])],"isStart":false})});}
            var Q8;
            Q8=makeQuery(id+"F2.opExtrude","CAP_EDGE",EDGE,{"disambiguationData":[OSD([sQuery(id+"F0.wireOp",EDGE,"E1.right")])],"isStart":false});
            var Q9;
            Q9=makeQuery(id+"F2.opExtrude","CAP_EDGE",EDGE,{"disambiguationData":[OSD([sQuery(id+"F0.wireOp",EDGE,"E1.top")])],"isStart":false});
            chamfer(context, id + "F41", {"entities" : qUnion([Q0, Q1, Q2, Q3, Q4, Q5, Q6, Q7, Q8, Q9]), "width" : 1 * mm, "tangentPropagation" : true});
        }
        {
            var Q0;
            Q0=makeQuery(id+"F38.opExtrude","SWEPT_FACE",FACE,{"disambiguationData":[OSD([sQuery(id+"F0.wireOp",EDGE,"E2.bottom")])]});
            var sketch = newSketch(context, id + "F42", { "sketchPlane" : qUnion([Q0])});
            skLineSegment(sketch, "E38", {"start": v(0, 3) * mm, "end": v(0, 2) * mm});
            skPoint(sketch, "E38.endSnap0", {"position": v(0, 3) * mm});
            skLineSegment(sketch, "E39.bottom", {"start": v(7.5, 1.05) * mm, "end": v(-7.5, 1.05) * mm});
            skLineSegment(sketch, "E39.top", {"start": v(7.5, 2.95) * mm, "end": v(-7.5, 2.95) * mm});
            skLineSegment(sketch, "E39.left", {"start": v(7.5, 1.05) * mm, "end": v(7.5, 2.95) * mm});
            skLineSegment(sketch, "E39.right", {"start": v(-7.5, 1.05) * mm, "end": v(-7.5, 2.95) * mm});
            skPoint(sketch, "E39.middle", {"position": v(0, 2) * mm});
            skSolve(sketch);
        }
        {
            var Q0;
            Q0=makeQuery(id+"F42.imprint","IMPRINT",FACE,{"disambiguationData":[TD([[makeQuery(id+"F42.imprint","IMPRINT",EDGE,{"derivedFrom":sQuery(id+"F42.wireOp",EDGE,"E39.bottom")}),-1.0]])]});
            extrude(context, id + "F43", {"entities" : qUnion([Q0]), "operationType" : NewBodyOperationType.ADD, "depth" : 1 * mm, "offsetDistance" : 25 * mm});
        }
        {
            var Q0;
            Q0=makeQuery(id+"F38.opExtrude","SWEPT_FACE",FACE,{"disambiguationData":[OSD([sQuery(id+"F0.wireOp",EDGE,"E2.right")])]});
            var sketch = newSketch(context, id + "F44", { "sketchPlane" : qUnion([Q0])});
            skLineSegment(sketch, "E40", {"start": v(100.04, 3) * mm, "end": v(100.04, 2) * mm});
            skLineSegment(sketch, "E41.bottom", {"start": v(107.04, 1.05) * mm, "end": v(93.04, 1.05) * mm});
            skLineSegment(sketch, "E41.top", {"start": v(107.04, 2.95) * mm, "end": v(93.04, 2.95) * mm});
            skLineSegment(sketch, "E41.left", {"start": v(107.04, 1.05) * mm, "end": v(107.04, 2.95) * mm});
            skLineSegment(sketch, "E41.right", {"start": v(93.04, 1.05) * mm, "end": v(93.04, 2.95) * mm});
            skPoint(sketch, "E41.middle", {"position": v(100.04, 2) * mm});
            skSolve(sketch);
        }
        {
            var Q0;
            Q0=makeQuery(id+"F44.imprint","IMPRINT",FACE,{"disambiguationData":[TD([[makeQuery(id+"F44.imprint","IMPRINT",EDGE,{"derivedFrom":sQuery(id+"F44.wireOp",EDGE,"E41.bottom")}),-1.0]])]});
            extrude(context, id + "F45", {"entities" : qUnion([Q0]), "operationType" : NewBodyOperationType.ADD, "depth" : 1 * mm, "offsetDistance" : 25 * mm});
        }
        {
            var Q0;
            Q0=makeQuery(id+"F38.opExtrude","SWEPT_FACE",FACE,{"disambiguationData":[OSD([sQuery(id+"F0.wireOp",EDGE,"E2.top")])]});
            var sketch = newSketch(context, id + "F46", { "sketchPlane" : qUnion([Q0])});
            skLineSegment(sketch, "E42", {"start": v(0, 3) * mm, "end": v(0, 2) * mm});
            skPoint(sketch, "E42.endSnap0", {"position": v(0, 3) * mm});
            skLineSegment(sketch, "E43.bottom", {"start": v(7.5, 1.05) * mm, "end": v(-7.5, 1.05) * mm});
            skLineSegment(sketch, "E43.top", {"start": v(7.5, 2.95) * mm, "end": v(-7.5, 2.95) * mm});
            skLineSegment(sketch, "E43.left", {"start": v(7.5, 1.05) * mm, "end": v(7.5, 2.95) * mm});
            skLineSegment(sketch, "E43.right", {"start": v(-7.5, 1.05) * mm, "end": v(-7.5, 2.95) * mm});
            skPoint(sketch, "E43.middle", {"position": v(0, 2) * mm});
            skSolve(sketch);
        }
        {
            var Q0;
            Q0=makeQuery(id+"F46.imprint","IMPRINT",FACE,{"disambiguationData":[TD([[makeQuery(id+"F46.imprint","IMPRINT",EDGE,{"derivedFrom":sQuery(id+"F46.wireOp",EDGE,"E43.bottom")}),-1.0]])]});
            extrude(context, id + "F47", {"entities" : qUnion([Q0]), "operationType" : NewBodyOperationType.ADD, "depth" : 1 * mm, "offsetDistance" : 25 * mm});
        }
        {
            var Q0;
            Q0=makeQuery(id+"F38.opExtrude","SWEPT_FACE",FACE,{"disambiguationData":[OSD([sQuery(id+"F0.wireOp",EDGE,"E2.left")])]});
            var sketch = newSketch(context, id + "F48", { "sketchPlane" : qUnion([Q0])});
            skLineSegment(sketch, "E44", {"start": v(-100.04, 3) * mm, "end": v(-100.04, 2) * mm});
            skLineSegment(sketch, "E45.bottom", {"start": v(-93.04, 1.05) * mm, "end": v(-107.04, 1.05) * mm});
            skLineSegment(sketch, "E45.top", {"start": v(-93.04, 2.95) * mm, "end": v(-107.04, 2.95) * mm});
            skLineSegment(sketch, "E45.left", {"start": v(-93.04, 1.05) * mm, "end": v(-93.04, 2.95) * mm});
            skLineSegment(sketch, "E45.right", {"start": v(-107.04, 1.05) * mm, "end": v(-107.04, 2.95) * mm});
            skPoint(sketch, "E45.middle", {"position": v(-100.04, 2) * mm});
            skSolve(sketch);
        }
        {
            var Q0;
            Q0=makeQuery(id+"F48.imprint","IMPRINT",FACE,{"disambiguationData":[TD([[makeQuery(id+"F48.imprint","IMPRINT",EDGE,{"derivedFrom":sQuery(id+"F48.wireOp",EDGE,"E45.bottom")}),-1.0]])]});
            extrude(context, id + "F49", {"entities" : qUnion([Q0]), "operationType" : NewBodyOperationType.ADD, "depth" : 1 * mm, "offsetDistance" : 25 * mm});
        }
        {
            var Q0;
            Q0=makeQuery(id+"F34.boolean.opBoolean","COPY",EDGE,{"derivedFrom":makeQuery(id+"F34.opExtrude","CAP_EDGE",EDGE,{"disambiguationData":[OSD([sQuery(id+"F20.wireOp",EDGE,"E26.bottom")])],"isStart":false})});
            var Q1;
            Q1=makeQuery(id+"F34.boolean.opBoolean","COPY",EDGE,{"derivedFrom":makeQuery(id+"F34.opExtrude","CAP_EDGE",EDGE,{"disambiguationData":[OSD([sQuery(id+"F20.wireOp",EDGE,"E26.top")])],"isStart":false})});
            var Q2;
            Q2=makeQuery(id+"F33.boolean.opBoolean","COPY",EDGE,{"derivedFrom":makeQuery(id+"F33.opExtrude","CAP_EDGE",EDGE,{"disambiguationData":[OSD([sQuery(id+"F8.wireOp",EDGE,"E14.bottom")])],"isStart":false})});
            var Q3;
            Q3=makeQuery(id+"F33.boolean.opBoolean","COPY",EDGE,{"derivedFrom":makeQuery(id+"F33.opExtrude","CAP_EDGE",EDGE,{"disambiguationData":[OSD([sQuery(id+"F8.wireOp",EDGE,"E14.top")])],"isStart":false})});
            var Q4;
            Q4=makeQuery(id+"F32.boolean.opBoolean","COPY",EDGE,{"derivedFrom":makeQuery(id+"F32.opExtrude","CAP_EDGE",EDGE,{"disambiguationData":[OSD([sQuery(id+"F24.wireOp",EDGE,"E34.bottom")])],"isStart":false})});
            var Q5;
            Q5=makeQuery(id+"F32.boolean.opBoolean","COPY",EDGE,{"derivedFrom":makeQuery(id+"F32.opExtrude","CAP_EDGE",EDGE,{"disambiguationData":[OSD([sQuery(id+"F24.wireOp",EDGE,"E34.top")])],"isStart":false})});
            var Q6;
            Q6=makeQuery(id+"F35.boolean.opBoolean","COPY",EDGE,{"derivedFrom":makeQuery(id+"F35.opExtrude","CAP_EDGE",EDGE,{"disambiguationData":[OSD([sQuery(id+"F14.wireOp",EDGE,"E21.bottom")])],"isStart":false})});
            var Q7;
            Q7=makeQuery(id+"F35.boolean.opBoolean","COPY",EDGE,{"derivedFrom":makeQuery(id+"F35.opExtrude","CAP_EDGE",EDGE,{"disambiguationData":[OSD([sQuery(id+"F14.wireOp",EDGE,"E21.top")])],"isStart":false})});
            var Q8;
            Q8=makeQuery(id+"F25.boolean.opBoolean","COPY",EDGE,{"derivedFrom":makeQuery(id+"F25.opExtrude","CAP_EDGE",EDGE,{"disambiguationData":[OSD([sQuery(id+"F24.wireOp",EDGE,"E28.bottom")])],"isStart":false})});
            var Q9;
            Q9=makeQuery(id+"F25.boolean.opBoolean","COPY",EDGE,{"derivedFrom":makeQuery(id+"F25.opExtrude","CAP_EDGE",EDGE,{"disambiguationData":[OSD([sQuery(id+"F24.wireOp",EDGE,"E28.right")])],"isStart":false})});
            var Q10;
            Q10=makeQuery(id+"F25.boolean.opBoolean","COPY",EDGE,{"derivedFrom":makeQuery(id+"F25.opExtrude","CAP_EDGE",EDGE,{"disambiguationData":[OSD([sQuery(id+"F24.wireOp",EDGE,"E28.left")])],"isStart":false})});
            var Q11;
            Q11=makeQuery(id+"F25.boolean.opBoolean","COPY",EDGE,{"derivedFrom":makeQuery(id+"F25.opExtrude","CAP_EDGE",EDGE,{"disambiguationData":[OSD([sQuery(id+"F24.wireOp",EDGE,"E28.top")])],"isStart":false})});
            var Q12;
            Q12=makeQuery(id+"F49.opExtrude","CAP_EDGE",EDGE,{"disambiguationData":[OSD([sQuery(id+"F48.wireOp",EDGE,"E45.bottom")])],"isStart":false});
            var Q13;
            Q13=makeQuery(id+"F49.opExtrude","CAP_EDGE",EDGE,{"disambiguationData":[OSD([sQuery(id+"F48.wireOp",EDGE,"E45.top")])],"isStart":false});
            var Q14;
            Q14=makeQuery(id+"F47.opExtrude","CAP_EDGE",EDGE,{"disambiguationData":[OSD([sQuery(id+"F46.wireOp",EDGE,"E43.top")])],"isStart":false});
            var Q15;
            Q15=makeQuery(id+"F47.opExtrude","CAP_EDGE",EDGE,{"disambiguationData":[OSD([sQuery(id+"F46.wireOp",EDGE,"E43.bottom")])],"isStart":false});
            var Q16;
            Q16=makeQuery(id+"F43.opExtrude","CAP_EDGE",EDGE,{"disambiguationData":[OSD([sQuery(id+"F42.wireOp",EDGE,"E39.top")])],"isStart":false});
            var Q17;
            Q17=makeQuery(id+"F43.opExtrude","CAP_EDGE",EDGE,{"disambiguationData":[OSD([sQuery(id+"F42.wireOp",EDGE,"E39.bottom")])],"isStart":false});
            var Q18;
            Q18=makeQuery(id+"F45.opExtrude","CAP_EDGE",EDGE,{"disambiguationData":[OSD([sQuery(id+"F44.wireOp",EDGE,"E41.bottom")])],"isStart":false});
            var Q19;
            Q19=makeQuery(id+"F45.opExtrude","CAP_EDGE",EDGE,{"disambiguationData":[OSD([sQuery(id+"F44.wireOp",EDGE,"E41.top")])],"isStart":false});
            fillet(context, id + "F50", {"entities" : qUnion([Q0, Q1, Q2, Q3, Q4, Q5, Q6, Q7, Q8, Q9, Q10, Q11, Q12, Q13, Q14, Q15, Q16, Q17, Q18, Q19]), "radius" : 1 * mm, "tangentPropagation" : true, "allowEdgeOverflow" : false});
        }
        {
            var Q0;
            Q0=makeQuery(id+"F2.opExtrude","CAP_FACE",FACE,{"disambiguationData":[OSD([sQuery(id+"F0.wireOp",EDGE,"E1.bottom"),sQuery(id+"F0.wireOp",EDGE,"E1.top"),sQuery(id+"F0.wireOp",EDGE,"E1.left"),sQuery(id+"F0.wireOp",EDGE,"E1.right")])],"isStart":false});
            var sketch = newSketch(context, id + "F51", { "sketchPlane" : qUnion([Q0])});
            skText(sketch, "E46", { "text": "Sous", "fontName": "OpenSans-Regular.ttf"});
            skText(sketch, "E47", { "text": "Vide", "fontName": "OpenSans-Regular.ttf"});
            const initialGuessF51  = {"E46": [-0.03573, 0.10791, 1, 0, 0.025], "E47": [-0.03573, 0.0751, 1, 0, 0.025]};
            skSetInitialGuess(sketch, initialGuessF51);
            skSolve(sketch);
        }
        {
            var Q0;
            Q0 = qSketchRegion(id + "F51", true);
            extrude(context, id + "F52", {"entities" : qUnion([Q0]), "operationType" : NewBodyOperationType.REMOVE, "oppositeDirection" : true, "depth" : 1 * mm, "offsetDistance" : 25 * mm});
        }
    });
